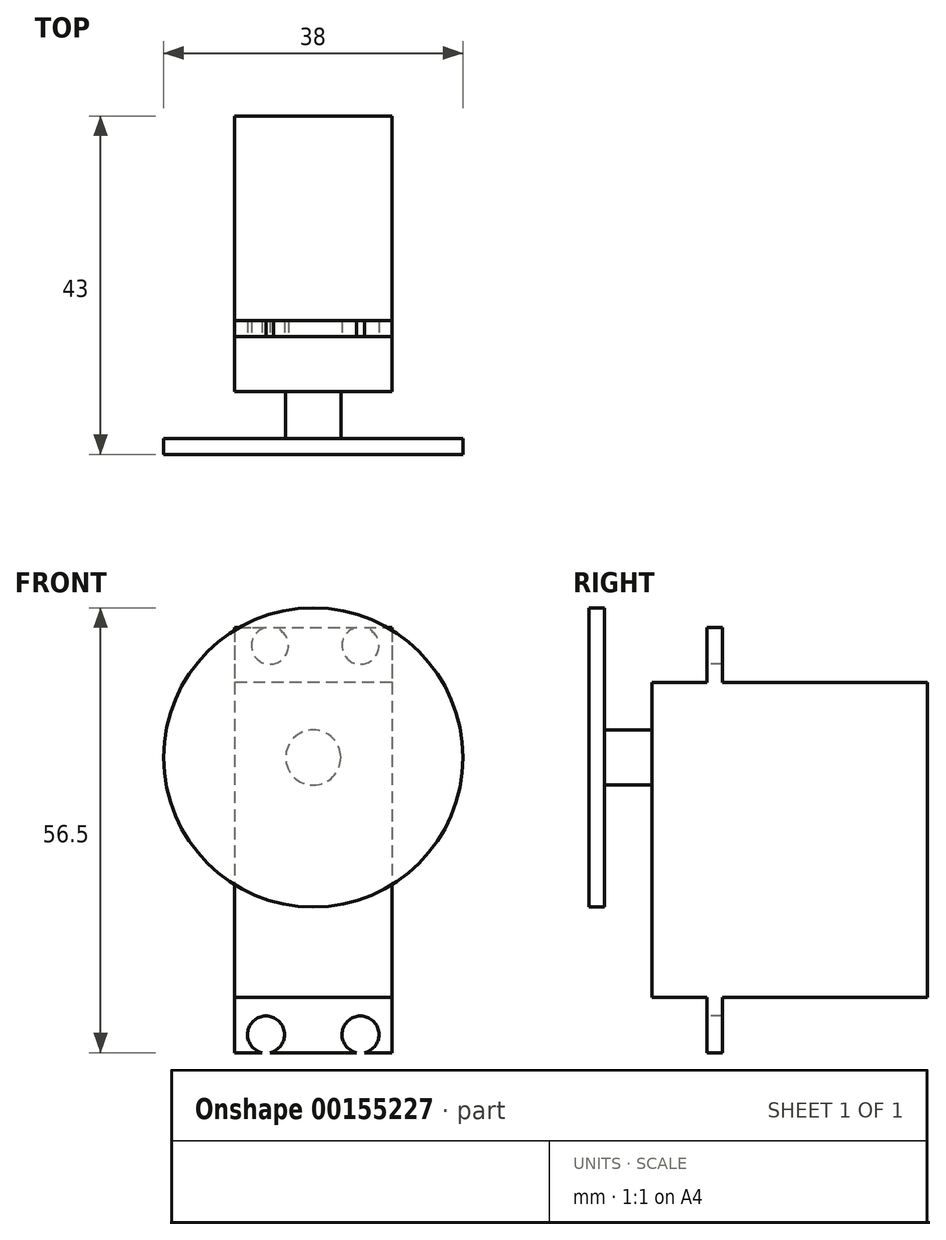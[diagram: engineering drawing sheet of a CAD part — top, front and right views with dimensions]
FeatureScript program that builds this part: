
annotation { "Feature Type Name" : "Feature", "Feature Type Description" : "" }
export const myFeature = defineFeature(function(context is Context, id is Id, definition is map)
    precondition{}
    {
        {
            var Q0;
            Q0=qCreatedBy(makeId("Front.planeOp"),FACE);
            var sketch = newSketch(context, id + "F0", { "sketchPlane" : qUnion([Q0])});
            skLineSegment(sketch, "E0.bottom", {"start": v(-10, 20) * mm, "end": v(10, 20) * mm});
            skLineSegment(sketch, "E0.top", {"start": v(-10, -20) * mm, "end": v(10, -20) * mm});
            skLineSegment(sketch, "E0.left", {"start": v(-10, 20) * mm, "end": v(-10, -20) * mm});
            skLineSegment(sketch, "E0.right", {"start": v(10, 20) * mm, "end": v(10, -20) * mm});
            skSolve(sketch);
        }
        {
            var Q0;
            Q0 = qSketchRegion(id + "F0", true);
            extrude(context, id + "F1", {"entities" : qUnion([Q0]), "endBound" : BoundingType.SYMMETRIC, "depth" : 35 * mm});
        }
        {
            var Q0;
            Q0=qCreatedBy(makeId("Top.planeOp"),FACE);
            var sketch = newSketch(context, id + "F2", { "sketchPlane" : qUnion([Q0])});
            skLineSegment(sketch, "E1.bottom", {"start": v(-10, -8.5) * mm, "end": v(10, -8.5) * mm});
            skLineSegment(sketch, "E1.top", {"start": v(-10, -10.5) * mm, "end": v(10, -10.5) * mm});
            skLineSegment(sketch, "E1.left", {"start": v(-10, -8.5) * mm, "end": v(-10, -10.5) * mm});
            skLineSegment(sketch, "E1.right", {"start": v(10, -8.5) * mm, "end": v(10, -10.5) * mm});
            skSolve(sketch);
        }
        {
            var Q0;
            Q0 = qSketchRegion(id + "F2", true);
            extrude(context, id + "F3", {"entities" : qUnion([Q0]), "operationType" : NewBodyOperationType.ADD, "endBound" : BoundingType.SYMMETRIC, "depth" : 54 * mm});
        }
        {
            var Q0;
            Q0=makeQuery(id+"F1.opExtrude","CAP_FACE",FACE,{"disambiguationData":[OSD([sQuery(id+"F0.wireOp",EDGE,"E0.bottom"),sQuery(id+"F0.wireOp",EDGE,"E0.top"),sQuery(id+"F0.wireOp",EDGE,"E0.left"),sQuery(id+"F0.wireOp",EDGE,"E0.right")])],"isStart":false});
            var sketch = newSketch(context, id + "F4", { "sketchPlane" : qUnion([Q0])});
            skCircle(sketch, "E2", {"center": v(0, 10.5) * mm, "radius": 3.5 * mm});
            skSolve(sketch);
        }
        {
            var Q0;
            Q0 = qSketchRegion(id + "F4", true);
            extrude(context, id + "F5", {"entities" : qUnion([Q0]), "operationType" : NewBodyOperationType.ADD, "depth" : 8 * mm});
        }
        {
            var Q0;
            Q0=makeQuery(id+"F5.opExtrude","CAP_FACE",FACE,{"disambiguationData":[OSD([sQuery(id+"F4.wireOp",EDGE,"E2")])],"isStart":false});
            var sketch = newSketch(context, id + "F6", { "sketchPlane" : qUnion([Q0])});
            skCircle(sketch, "E3", {"center": v(0, 10.5) * mm, "radius": 19 * mm});
            skSolve(sketch);
        }
        {
            var Q0;
            Q0 = qSketchRegion(id + "F6", true);
            extrude(context, id + "F7", {"entities" : qUnion([Q0]), "operationType" : NewBodyOperationType.ADD, "oppositeDirection" : true, "depth" : 2 * mm});
        }
        {
            var Q0;
            {var subQ2=sQuery(id+"F2.wireOp",EDGE,"E1.top");Q0=makeQuery(id+"F3.boolean.opBoolean","SPLIT",FACE,{"disambiguationData":[TD([makeQuery(id+"F1.opExtrude","SWEPT_FACE",FACE,{"disambiguationData":[OSD([sQuery(id+"F0.wireOp",EDGE,"E0.top")])]})])],"derivedFrom":makeQuery(id+"F3.opExtrude","SWEPT_FACE",FACE,{"disambiguationData":[OSD([subQ2])]})});}
            var sketch = newSketch(context, id + "F8", { "sketchPlane" : qUnion([Q0])});
            skCircle(sketch, "E4", {"center": v(-6, -24.7) * mm, "radius": 2.35 * mm});
            skCircle(sketch, "E5", {"center": v(6, -24.7) * mm, "radius": 2.35 * mm});
            skCircle(sketch, "E6", {"center": v(-5.5, 24.7) * mm, "radius": 2.35 * mm});
            skCircle(sketch, "E7", {"center": v(6, 24.7) * mm, "radius": 2.35 * mm});
            skSolve(sketch);
        }
        {
            var Q0;
            Q0 = qSketchRegion(id + "F8", true);
            extrude(context, id + "F9", {"entities" : qUnion([Q0]), "operationType" : NewBodyOperationType.REMOVE, "oppositeDirection" : true, "depth" : 25.4 * mm});
        }
    });
